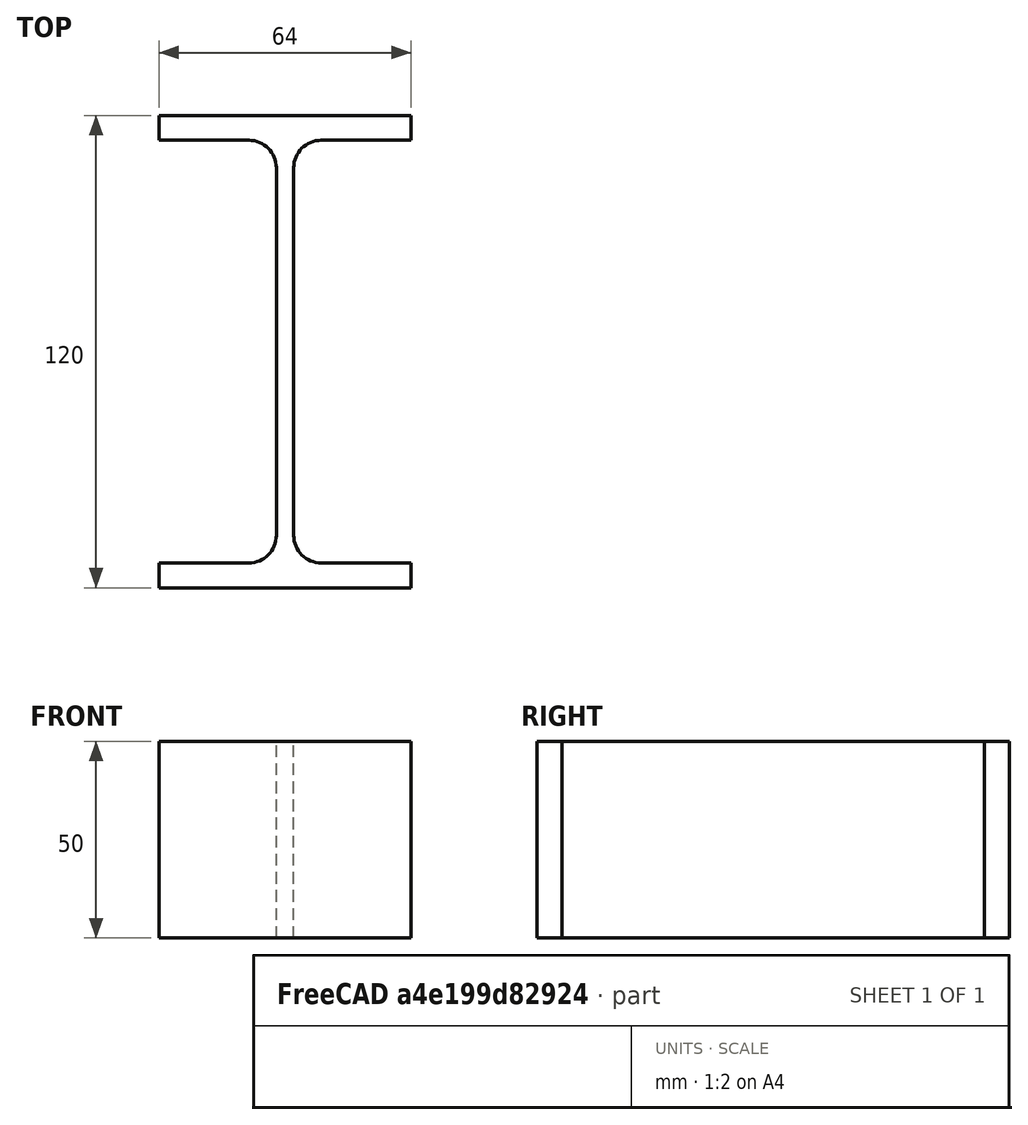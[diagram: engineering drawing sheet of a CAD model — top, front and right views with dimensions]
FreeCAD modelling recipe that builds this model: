
FCSTD DOCUMENT  (FreeCAD 0.15R4671 (Git))
Label: IPE-Profile 120 DIN1025-5 S235JR
License: All rights reserved
LicenseURL: http://en.wikipedia.org/wiki/All_rights_reserved
objects: Sketcher::SketchObject×1, Part::Extrusion×1
note: 2 computed .brp shape members not serialized (recipe doc carries the construction recipe); baked Part::Feature solids carry a one-line shape summary decoded from their .brp

FEATURE [Sketcher::SketchObject] Sketch
  sketch-geometry (16):
    g0: LineSegment StartX=2.2 StartY=-46.7 StartZ=0 EndX=2.2 EndY=46.7 EndZ=0
    g1: LineSegment StartX=9.2 StartY=53.7 StartZ=0 EndX=32 EndY=53.7 EndZ=0
    g2: LineSegment StartX=32 StartY=53.7 StartZ=0 EndX=32 EndY=60 EndZ=0
    g3: LineSegment StartX=32 StartY=60 StartZ=0 EndX=-32 EndY=60 EndZ=0
    g4: LineSegment StartX=-32 StartY=60 StartZ=0 EndX=-32 EndY=53.7 EndZ=0
    g5: LineSegment StartX=-32 StartY=53.7 StartZ=0 EndX=-9.2 EndY=53.7 EndZ=0
    g6: LineSegment StartX=-2.2 StartY=46.7 StartZ=0 EndX=-2.2 EndY=-46.7 EndZ=0
    g7: LineSegment StartX=-9.2 StartY=-53.7 StartZ=0 EndX=-32 EndY=-53.7 EndZ=0
    g8: LineSegment StartX=-32 StartY=-53.7 StartZ=0 EndX=-32 EndY=-60 EndZ=0
    g9: LineSegment StartX=-32 StartY=-60 StartZ=0 EndX=32 EndY=-60 EndZ=0
    g10: LineSegment StartX=32 StartY=-60 StartZ=0 EndX=32 EndY=-53.7 EndZ=0
    g11: LineSegment StartX=32 StartY=-53.7 StartZ=0 EndX=9.2 EndY=-53.7 EndZ=0
    g12: ArcOfCircle CenterX=9.2 CenterY=46.7 CenterZ=0 NormalX=0 NormalY=0 NormalZ=1 Radius=7 StartAngle=1.5708 EndAngle=3.14159
    g13: ArcOfCircle CenterX=9.2 CenterY=-46.7 CenterZ=0 NormalX=0 NormalY=0 NormalZ=1 Radius=7 StartAngle=3.14159 EndAngle=4.71239
    g14: ArcOfCircle CenterX=-9.2 CenterY=46.7 CenterZ=0 NormalX=0 NormalY=0 NormalZ=1 Radius=7 StartAngle=0 EndAngle=1.5708
    g15: ArcOfCircle CenterX=-9.2 CenterY=-46.7 CenterZ=0 NormalX=0 NormalY=0 NormalZ=1 Radius=7 StartAngle=4.71239 EndAngle=6.28319
  constraints (42):
    c: Vertical(g0)
    c: Coincident(g2,g1)
    c: Vertical(g2)
    c: Coincident(g3,g2)
    c: Coincident(g4,g3)
    c: Vertical(g4)
    c: Coincident(g5,g4)
    c: Horizontal(g5)
    c: Vertical(g6)
    c: Horizontal(g7)
    c: Coincident(g8,g7)
    c: Vertical(g8)
    c: Coincident(g9,g8)
    c: Horizontal(g9)
    c: Coincident(g10,g9)
    c: Vertical(g10)
    c: Coincident(g11,g10)
    c: Horizontal(g11)
    c: Tangent(g1,g12) = 1.5708
    c: Tangent(g0,g12) = 1.5708
    c: Tangent(g0,g13) = 1.5708
    c: Tangent(g11,g13) = 1.5708
    c: Tangent(g5,g14) = 1.5708
    c: Tangent(g6,g14) = 1.5708
    c: Tangent(g6,g15) = 1.5708
    c: Tangent(g7,g15) = 1.5708
    c: Equal(g3,g9)
    c: Equal(g2,g4)
    c: Equal(g4,g8)
    c: Equal(g8,g10)
    c: Equal(g12,g14)
    c: Equal(g14,g15)
    c: Equal(g15,g13)
    c: Symmetric(g2,g3,g-2)
    c: Symmetric(g9,g8,g-2)
    c: Symmetric(g0,g6,g-2)
    c: Symmetric(g2,g9,g-1)
    c: DistanceY(g2,g9) = -120
    c: DistanceX(g3) = -64
    c: DistanceX(g0,g6) = -4.4
    c: DistanceY(g2) = 6.3
    c: Radius(g12) = 7
FEATURE [Part::Extrusion] Extrude  label="IPE-Profile 120 DIN1025-5 S235JR"
  Base = -> Sketch
  Dir = (0,0,50)
  Solid = true
